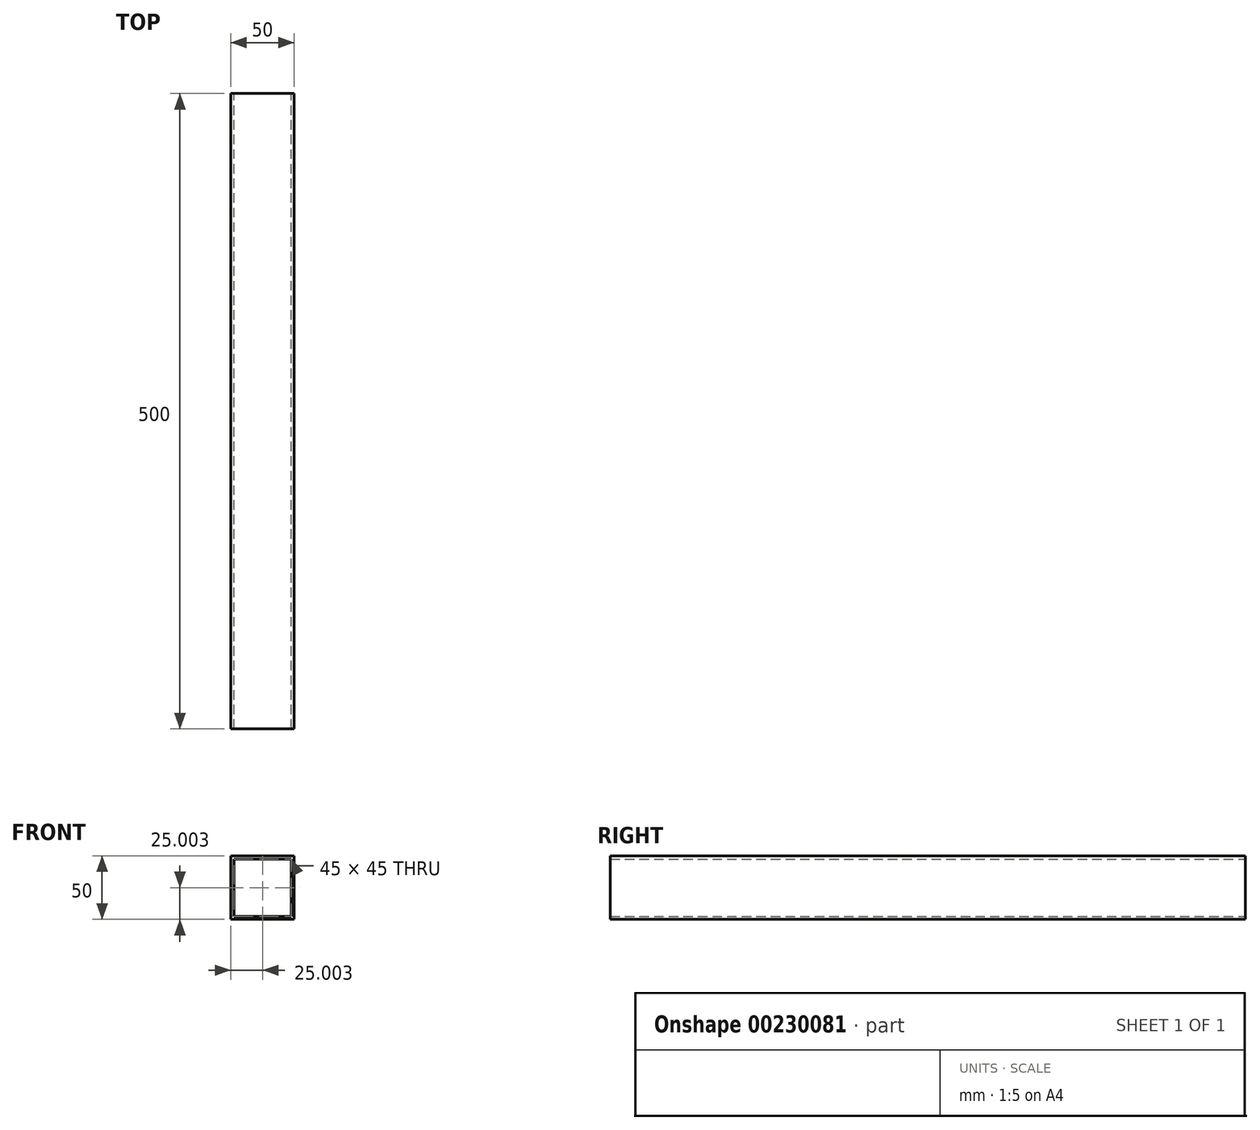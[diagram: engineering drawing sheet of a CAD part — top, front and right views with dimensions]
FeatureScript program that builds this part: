
annotation { "Feature Type Name" : "Feature", "Feature Type Description" : "" }
export const myFeature = defineFeature(function(context is Context, id is Id, definition is map)
    precondition{}
    {
        {
            var Q0;
            Q0=qCreatedBy(makeId("Front.planeOp"),FACE);
            var sketch = newSketch(context, id + "F0", { "sketchPlane" : qUnion([Q0])});
            skLineSegment(sketch, "E0.bottom", {"start": v(-36.89, 45.12) * mm, "end": v(13.11, 45.12) * mm});
            skLineSegment(sketch, "E0.top", {"start": v(-36.89, -4.88) * mm, "end": v(13.11, -4.88) * mm});
            skLineSegment(sketch, "E0.left", {"start": v(-36.89, 45.12) * mm, "end": v(-36.89, -4.88) * mm});
            skLineSegment(sketch, "E0.right", {"start": v(13.11, 45.12) * mm, "end": v(13.11, -4.88) * mm});
            skLineSegment(sketch, "E1.bottom", {"start": v(-34.39, 42.62) * mm, "end": v(10.61, 42.62) * mm});
            skLineSegment(sketch, "E1.top", {"start": v(-34.39, -2.38) * mm, "end": v(10.61, -2.38) * mm});
            skLineSegment(sketch, "E1.left", {"start": v(-34.39, 42.62) * mm, "end": v(-34.39, -2.38) * mm});
            skLineSegment(sketch, "E1.right", {"start": v(10.61, 42.62) * mm, "end": v(10.61, -2.38) * mm});
            skSolve(sketch);
        }
        {
            var Q0;
            Q0 = qSketchRegion(id + "F0", true);
            extrude(context, id + "F1", {"entities" : qUnion([Q0]), "endBound" : BoundingType.SYMMETRIC, "depth" : 500 * mm});
        }
    });
